# Revit family: MechanicalEquipment_HotWater_Rheem_TankpakSeries2_TPI018-B
name_source: partatom
category: Mechanical Equipment
units: mm (PartAtom-declared; Revit-internal decimal feet)

## family parameters
Always vertical = Yes
Cut with Voids When Loaded = No
Part Type = Normal
Room Calculation Point = No
Round Connector Dimension = Use Diameter
Shared = No
Work Plane-Based = No

## types (2) — shared parameters
ApparentLoad_ANZRS = 4440 VA
Assembly Code = D3020100
BaseToController = 1000 mm  [stored 3.28084 ft]
BaseToGPO = 850 mm
ClearanceZoneWidth = 600 mm
ColdPipeDescription = Cold Water In
ColdPipeRadius = 33 mm
ColdPipeSize = 65 mm  [stored 0.213255 ft]
ControllerConnectorDescription = Electrical Connector
ControllerHeight = 300 mm
ControllerMaterial = Controller Material
ControllerTextMaterial = Controller Text Material
Description = Tankpak Series 2 internal 18 Back to Back
ElectricalConnectionInformation = Each water heater is supplied with a 1.8 metre lead and plug and requires a 240 V 50 Hz switched general purpose outlet (GPO) to be located within 1.2 metres of the installation. The GPO must be clear of the flue exhaust, draining water, gas supply pipe and water connections. The GPO must be suitable for outdoor installation if installed outdoors.
ElectricalConnectionType = Hard Wired Conduit Connection
ElectricalPowerConsumption = 80 Watts - 872/862 series - Burner on. anti-frost device inactive;175 Watts - 872627 (outdoor) - Burner on. anti-frost device active;187 Watts - 862627 (indoor) - Burner on. anti-frost device active.
FirstHourCapacity = 16040 l
FloorMountHeight = 1741 mm  [stored 5.71194 ft]
FlueDescription = Certified Rheem coaxial flue components must be used.
FlueDiameter = 127 mm  [stored 0.416667 ft]
FlueTankMaterial = Flue Tank Material
FrameMaterial = Frame Material
FrameThickness = 160 mm
Frequency_ANZRS = 50 Hz
GasPipeSize = 80 mm  [stored 0.262467 ft]
GasXReference = 441 mm  [stored 1.44685 ft]
GasYReference = 269 mm
GpoHeight = 300 mm
GpoMaterial = Gpo Material
HotPipeDescription = Hot Water Out
HotPipeSize = 65 mm  [stored 0.213255 ft]
HotXReference = 401 mm  [stored 1.31562 ft]
HotYReference = 392 mm  [stored 1.28609 ft]
Manufacturer = Rheem
Model = TPI18
ModifiedIssue_ANZRS = 20141010.54 $
PowerFactor_ANZRS = 1
PumpLength = 300 mm
PumpMaterial = Pump Material
PumpRadius = 85 mm  [stored 0.278871 ft]
PumpYReference = 160 mm
RecommendedStorage = 3 x 610430@410L
RowLength = 1115 mm
StandThickness = 90 mm
TankCentreXReference = 380 mm
TankDistance = 600 mm
TankHeight = 500 mm
TankThickness = 220 mm
TankWidth = 350 mm  [stored 1.14829 ft]
ThermalInput_PerHour = 3690000000 J
TopOfFrame = 1626 mm  [stored 5.33465 ft]
Type Comments = 14809L/hr Recovery @ 50˚C rise
URL = http://www.rheem.com.au
UnitType = Indoor
Voltage = 240 V
WallMountHeight = 1793 mm
Weight(kg) = 776
Width = 3346 mm  [stored 10.9777 ft]

## per-type parameters (varying)
| type | GasPipeDescription | PumpXReference |
| TPI18NBD | Propane Gas | 571 mm |
| TPI18PBD | Propane gas | 573 mm |

note: [stored X ft] marks values corroborated as IEEE doubles in the binary element streams (Revit-internal decimal feet)

## geometry (parser evidence)
native form markers: Sweep x5
no freeform markers — native parametric forms only
